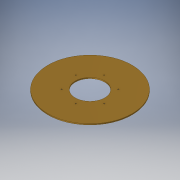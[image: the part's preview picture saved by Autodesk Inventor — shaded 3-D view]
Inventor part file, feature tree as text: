
AUTODESK INVENTOR PART (.ipt)
format: ipt  version: 2018 (Build 220112000, 112)  size: 116,736 bytes
history: native  units: in
note: dims shown in document units (in); Inventor stores cm internally (conversion verified against a paired STEP export)
features: sketch x2, extrude x1, hole x1, pattern_circular x1
ambient origin geometry x8: Origin, YZ Plane, XZ Plane, XY Plane, X Axis, Y Axis, Z Axis, Center Point
bodies: Solid1 (feature_tree)
feature tree (5):
  extrude  "Extrusion1"  Depth=0.1in TaperAngle=0.0deg
  hole  "Hole1"  [1 undecoded]
  pattern_circular  "Circular Pattern1"  Count=6 Angle=360.0deg
  sketch  "Sketch1"  dims[d0=7.85in d2=0.1in d3=0.0in]
  sketch  "Sketch2"  dims[d4=1.875in d5=45.0deg d6=0.112in d7=0.276in d8=0.375in d9=0.25in d10=0.5635in d11=0.41in d12=0.8108in d13=2.3622in d14=360.0deg d16=2.75in]
note: 1 required parameter value undecoded (feature->parameter linkage not recoverable at this tier; creation-order binding heuristic only, values carry confidence <= 0.55)
